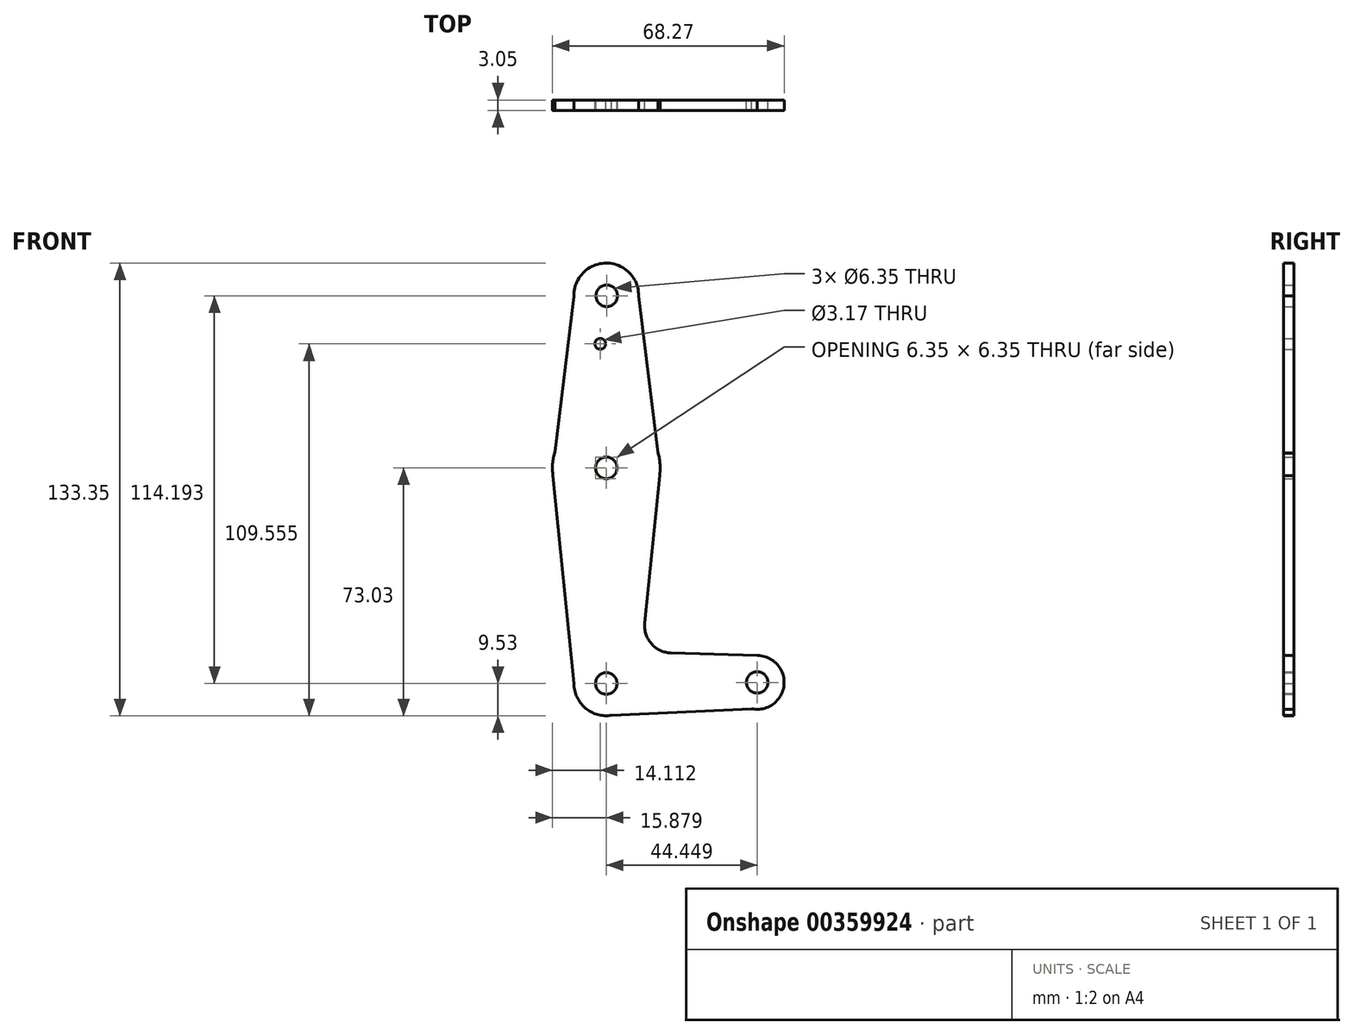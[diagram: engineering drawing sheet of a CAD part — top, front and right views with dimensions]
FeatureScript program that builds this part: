
annotation { "Feature Type Name" : "Feature", "Feature Type Description" : "" }
export const myFeature = defineFeature(function(context is Context, id is Id, definition is map)
    precondition{}
    {
        {
            var Q0;
            Q0=qCreatedBy(makeId("Front.planeOp"),FACE);
            var sketch = newSketch(context, id + "F0", { "sketchPlane" : qUnion([Q0])});
            skCircle(sketch, "E0", {"center": v(-26.54, 67.1) * mm, "radius": 9.52 * mm});
            skCircle(sketch, "E1", {"center": v(-26.54, 16.3) * mm, "radius": 15.88 * mm});
            skCircle(sketch, "E2", {"center": v(17.9, -46.9) * mm, "radius": 7.94 * mm});
            skCircle(sketch, "E3", {"center": v(-26.54, -47.2) * mm, "radius": 9.53 * mm});
            skLineSegment(sketch, "E4", {"start": v(-26.54, 67.1) * mm, "end": v(-26.54, 16.3) * mm});
            skLineSegment(sketch, "E5", {"start": v(-17.02, 66.97) * mm, "end": v(-10.67, 15.82) * mm});
            skLineSegment(sketch, "E6", {"start": v(-10.84, 13.95) * mm, "end": v(-15.2, -29.48) * mm});
            skLineSegment(sketch, "E7", {"start": v(17.97, -38.96) * mm, "end": v(-7.51, -38.21) * mm});
            skLineSegment(sketch, "E8", {"start": v(-27.2, -56.7) * mm, "end": v(20.26, -54.48) * mm});
            skLineSegment(sketch, "E9", {"start": v(-36.06, 66.85) * mm, "end": v(-42.4, 15.46) * mm});
            skCircle(sketch, "E10", {"center": v(-26.54, 16.3) * mm, "radius": 3.18 * mm});
            skCircle(sketch, "E11", {"center": v(-26.41, 67) * mm, "radius": 3.18 * mm});
            skCircle(sketch, "E12", {"center": v(-26.54, -47.2) * mm, "radius": 3.18 * mm});
            skCircle(sketch, "E13", {"center": v(17.9, -46.9) * mm, "radius": 3.18 * mm});
            skArc(sketch, "E14.filletArc", {"start": v(-15.2, -29.48) * mm, "mid": v(-13.25, -35.52) * mm, "end": v(-7.51, -38.21) * mm});
            skCircle(sketch, "E15", {"center": v(-28.3, 52.83) * mm, "radius": 1.59 * mm});
            skLineSegment(sketch, "E16", {"start": v(-42.24, 13.95) * mm, "end": v(-36.07, -47.2) * mm});
            skLineSegment(sketch, "E17", {"start": v(-26.54, -47.2) * mm, "end": v(17.9, -46.9) * mm});
            skLineSegment(sketch, "E18", {"start": v(-26.54, 16.3) * mm, "end": v(-26.54, -47.2) * mm});
            skSolve(sketch);
        }
        {
            var Q0;
            Q0 = qSketchRegion(id + "F0", true);
            var Q1;
            {var subQ0=sQuery(id+"F0.wireOp",EDGE,"E18");var subQ1=sQuery(id+"F0.wireOp",EDGE,"E3");var subQ2=makeQuery(id+"F0.imprint","INTERSECT",VERTEX,{"derivedFrom":[subQ1,subQ0]});Q1=makeQuery(id+"F0.imprint","IMPRINT",FACE,{"disambiguationData":[TD([[makeQuery(id+"F0.imprint","IMPRINT",EDGE,{"disambiguationData":[TD([[subQ2,1.0]])],"derivedFrom":subQ1}),1.0]])]});}
            extrude(context, id + "F1", {"entities" : qUnion([Q0, Q1]), "depth" : 3.05 * mm});
        }
    });
